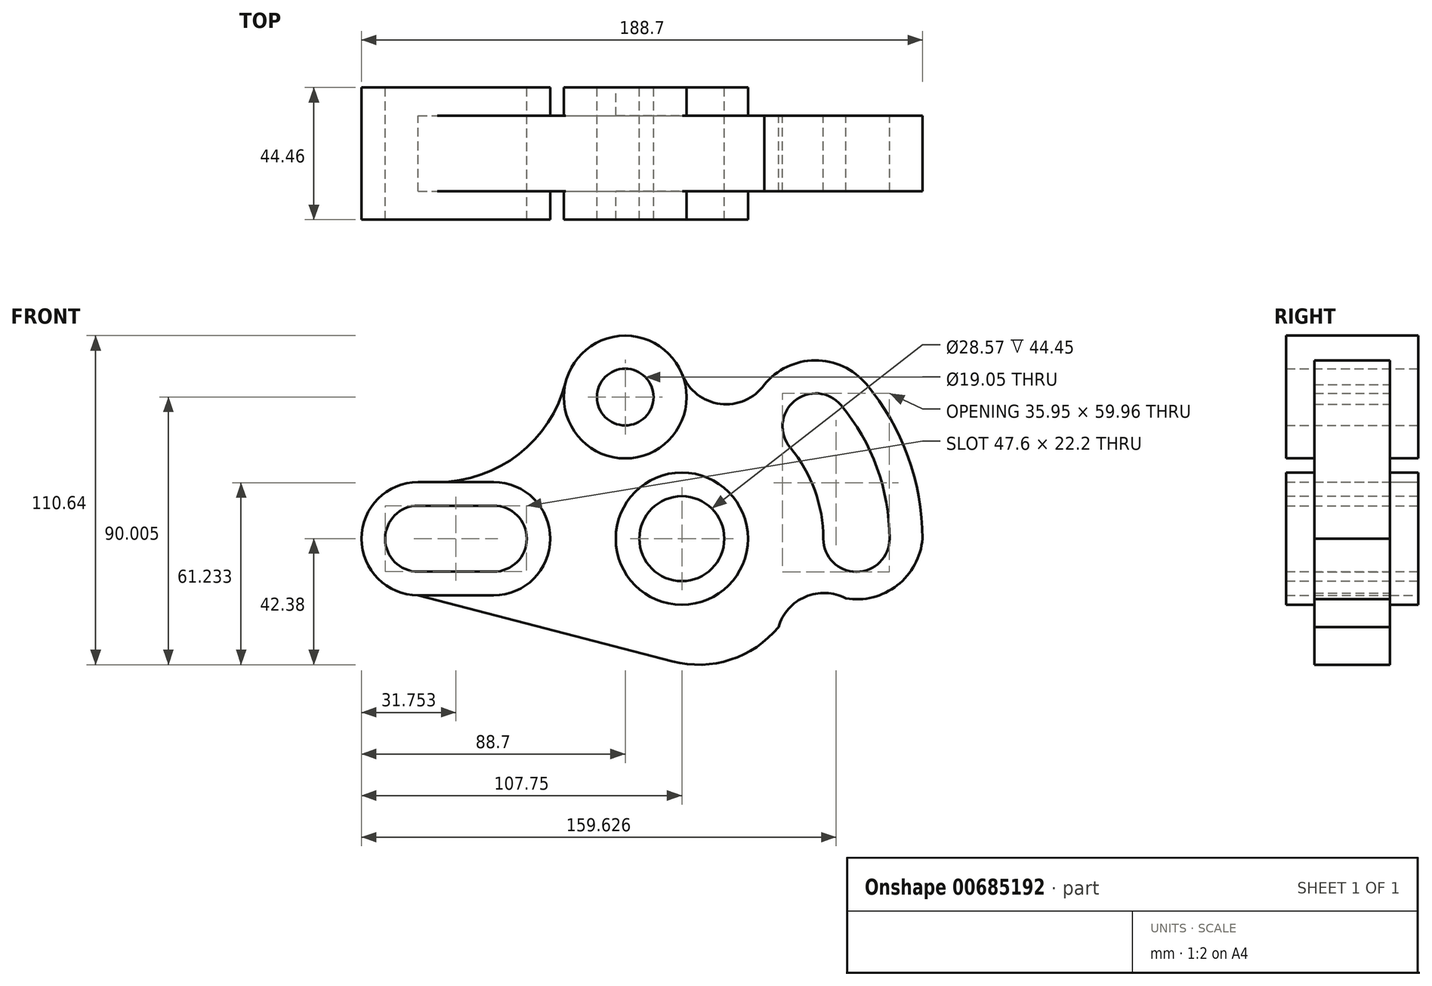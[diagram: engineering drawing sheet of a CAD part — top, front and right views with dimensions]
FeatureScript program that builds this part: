
annotation { "Feature Type Name" : "Feature", "Feature Type Description" : "" }
export const myFeature = defineFeature(function(context is Context, id is Id, definition is map)
    precondition{}
    {
        {
            var Q0;
            Q0=qCreatedBy(makeId("Front.planeOp"),FACE);
            var sketch = newSketch(context, id + "F0", { "sketchPlane" : qUnion([Q0])});
            skCircle(sketch, "E0", {"center": v(0, 0) * mm, "radius": 14.29 * mm});
            skCircle(sketch, "E1", {"center": v(0, 0) * mm, "radius": 22.23 * mm});
            skLineSegment(sketch, "E2", {"start": v(-135.59, 0) * mm, "end": v(102.78, 0) * mm, "construction": true});
            skLineSegment(sketch, "E3", {"start": v(0, 0) * mm, "end": v(85.5, 71.74) * mm, "construction": true});
            skArc(sketch, "E4", {"start": v(58.72, 0) * mm, "mid": v(55.18, 20.09) * mm, "end": v(44.99, 37.75) * mm, "construction": true});
            skLineSegment(sketch, "E5", {"start": v(-88.7, 30.12) * mm, "end": v(-88.7, -23.54) * mm, "construction": true});
            skLineSegment(sketch, "E6", {"start": v(-63.3, 31) * mm, "end": v(-63.3, -23.32) * mm, "construction": true});
            skArc(sketch, "E7", {"start": v(-88.7, 11.1) * mm, "mid": v(-99.8, 0) * mm, "end": v(-88.7, -11.1) * mm});
            skPoint(sketch, "E8", {"position": v(-63.3, 0) * mm});
            skArc(sketch, "E9", {"start": v(-63.3, -11.1) * mm, "mid": v(-52.2, 0) * mm, "end": v(-63.3, 11.1) * mm});
            skLineSegment(sketch, "E10", {"start": v(-88.7, 11.1) * mm, "end": v(-63.3, 11.1) * mm});
            skLineSegment(sketch, "E11", {"start": v(-88.7, -11.1) * mm, "end": v(-63.3, -11.1) * mm});
            skLineSegment(sketch, "E12.0", {"start": v(-88.7, 19.05) * mm, "end": v(-63.3, 19.05) * mm});
            skArc(sketch, "E12.1", {"start": v(-88.7, 19.05) * mm, "mid": v(-107.75, 0) * mm, "end": v(-88.7, -19.05) * mm});
            skLineSegment(sketch, "E12.2", {"start": v(-88.7, -19.05) * mm, "end": v(-63.3, -19.05) * mm});
            skArc(sketch, "E12.3", {"start": v(-63.3, -19.05) * mm, "mid": v(-44.25, 0) * mm, "end": v(-63.3, 19.05) * mm});
            skArc(sketch, "E13", {"start": v(47.6, 0) * mm, "mid": v(58.72, -11.13) * mm, "end": v(69.85, 0) * mm});
            skArc(sketch, "E14", {"start": v(53.5, 44.9) * mm, "mid": v(37.83, 46.27) * mm, "end": v(36.46, 30.6) * mm});
            skArc(sketch, "E15", {"start": v(47.6, 0) * mm, "mid": v(44.73, 16.28) * mm, "end": v(36.46, 30.6) * mm});
            skArc(sketch, "E16", {"start": v(69.85, 0) * mm, "mid": v(65.64, 23.9) * mm, "end": v(53.5, 44.9) * mm});
            skArc(sketch, "E17", {"start": v(40.06, -42.94) * mm, "mid": v(57.66, 11.14) * mm, "end": v(21.2, 54.77) * mm, "construction": true});
            skCircle(sketch, "E18", {"center": v(-19.05, 47.63) * mm, "radius": 9.53 * mm});
            skCircle(sketch, "E19", {"center": v(-19.05, 47.63) * mm, "radius": 20.64 * mm});
            skArc(sketch, "E20", {"start": v(-82.17, 19.05) * mm, "mid": v(-54.84, 28.45) * mm, "end": v(-39.06, 52.66) * mm});
            skArc(sketch, "E21", {"start": v(0.13, 55.23) * mm, "mid": v(12.9, 45.34) * mm, "end": v(27.74, 51.76) * mm});
            skArc(sketch, "E22", {"start": v(62.01, 52.03) * mm, "mid": v(44.8, 59.97) * mm, "end": v(27.74, 51.76) * mm});
            skArc(sketch, "E23", {"start": v(80.95, 0) * mm, "mid": v(76.07, 27.69) * mm, "end": v(62.01, 52.03) * mm});
            skArc(sketch, "E24", {"start": v(55.18, -20.09) * mm, "mid": v(72.47, -15.69) * mm, "end": v(80.95, 0) * mm});
            skPoint(sketch, "E24.startSnap0", {"position": v(55.18, 20.09) * mm});
            skLineSegment(sketch, "E25", {"start": v(-88.7, -19.05) * mm, "end": v(-3.16, -41.26) * mm});
            skArc(sketch, "E26", {"start": v(55.18, -20.09) * mm, "mid": v(41.58, -19.52) * mm, "end": v(32.54, -29.7) * mm});
            skArc(sketch, "E27", {"start": v(-3.16, -41.26) * mm, "mid": v(16.38, -40.68) * mm, "end": v(32.54, -29.7) * mm});
            skSolve(sketch);
        }
        {
            var Q0;
            Q0=makeQuery(id+"F0.imprint","IMPRINT",FACE,{"disambiguationData":[TD([[makeQuery(id+"F0.imprint","IMPRINT",EDGE,{"derivedFrom":sQuery(id+"F0.wireOp",EDGE,"E1")}),-1.0]])]});
            extrude(context, id + "F1", {"entities" : qUnion([Q0]), "endBound" : BoundingType.SYMMETRIC, "depth" : 25.4 * mm, "offsetDistance" : 25.4 * mm});
        }
        {
            var Q0;
            Q0=makeQuery(id+"F0.imprint","IMPRINT",FACE,{"disambiguationData":[TD([[makeQuery(id+"F0.imprint","IMPRINT",EDGE,{"derivedFrom":sQuery(id+"F0.wireOp",EDGE,"E18")}),-1.0]])]});
            var Q1;
            Q1=makeQuery(id+"F0.imprint","IMPRINT",FACE,{"disambiguationData":[TD([[makeQuery(id+"F0.imprint","IMPRINT",EDGE,{"derivedFrom":sQuery(id+"F0.wireOp",EDGE,"E7")}),-1.0]])]});
            var Q2;
            Q2=makeQuery(id+"F0.imprint","IMPRINT",FACE,{"disambiguationData":[TD([[makeQuery(id+"F0.imprint","IMPRINT",EDGE,{"derivedFrom":sQuery(id+"F0.wireOp",EDGE,"E0")}),-1.0]])]});
            extrude(context, id + "F2", {"entities" : qUnion([Q0, Q1, Q2]), "operationType" : NewBodyOperationType.ADD, "endBound" : BoundingType.SYMMETRIC, "depth" : 44.45 * mm, "offsetDistance" : 25.4 * mm});
        }
    });
